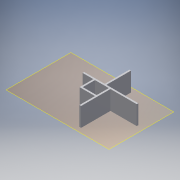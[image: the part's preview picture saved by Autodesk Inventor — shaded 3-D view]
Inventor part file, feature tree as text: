
AUTODESK INVENTOR PART (.ipt)
format: ipt  version: 2017 (Build 210142000, 142)  size: 177,152 bytes
history: native  units: mm
features: extrude x5, sketch x5, projected_geometry x4, other x3, plane x1, reference x1
ambient origin geometry x8: Origin, YZ Plane, XZ Plane, XY Plane, X Axis, Y Axis, Z Axis, Center Point
bodies: Body1 (feature_tree)
feature tree (19):
  plane  "Arbeitsebene1"
  extrude  "Extrusion4"  Depth=200.0mm
  extrude  "Extrusion5"  Depth=200.0mm
  extrude  "Extrusion6"  Depth=200.0mm
  extrude  "Extrusion7"  Depth=2500.0mm
  extrude  "Extrusion8"  Depth=200.0mm
  sketch  "Skizze1"  dims[d0=200.0mm d1=200.0mm]
  reference  "Referenz1"
  sketch  "Skizze4"  dims[d2=200.0mm d3=200.0mm]
  projected_geometry  "Projizierte Kontur3"
  sketch  "Skizze5"  dims[d4=2980.0mm d5=200.0mm d6=200.0mm]
  projected_geometry  "Projizierte Kontur4"
  sketch  "Skizze6"  dims[d8=200.0mm d9=2500.0mm]
  projected_geometry  "Projizierte Kontur5"
  sketch  "Skizze7"  dims[d16=3880.0mm d26=200.0mm d27=200.0mm d28=1310.0mm d29=200.0mm d30=1500.0mm d31=1680.0mm d32=2300.0mm d33=0.0mm d34=950.0mm d35=1900.0mm d36=2300.0mm d37=0.0mm d38=950.0mm d39=1900.0mm d40=2300.0mm d41=0.0mm d42=950.0mm d43=1900.0mm d44=2300.0mm d45=0.0mm d46=950.0mm d47=1900.0mm d48=2300.0mm d49=0.0mm]
  projected_geometry  "Projizierte Kontur6"
  other  "<userpath>\Documents\Inventor\Oli_Grundstück\Haus.iam"
  other  "Haus.iam"
  other  "Zwischendecke:1"
